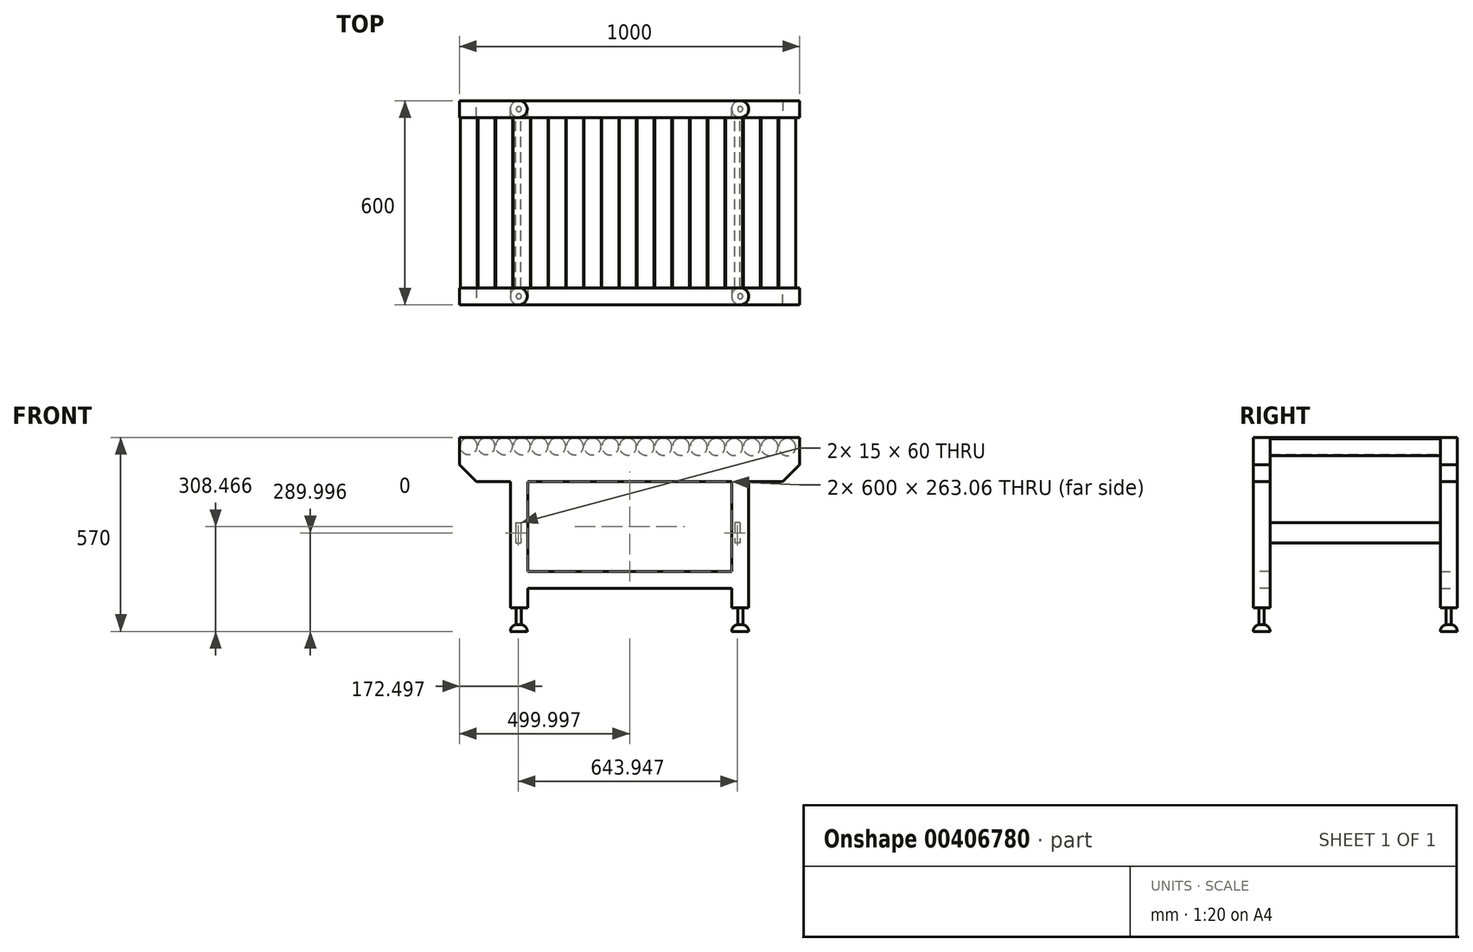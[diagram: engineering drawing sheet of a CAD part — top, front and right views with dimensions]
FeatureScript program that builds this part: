
annotation { "Feature Type Name" : "Feature", "Feature Type Description" : "" }
export const myFeature = defineFeature(function(context is Context, id is Id, definition is map)
    precondition{}
    {
        {
            var Q0;
            Q0=qCreatedBy(makeId("Front.planeOp"),FACE);
            var sketch = newSketch(context, id + "F0", { "sketchPlane" : qUnion([Q0])});
            skLineSegment(sketch, "E0", {"start": v(-494.47, 46.27) * mm, "end": v(505.53, 46.27) * mm});
            skLineSegment(sketch, "E1", {"start": v(505.53, 46.27) * mm, "end": v(505.53, -83.73) * mm});
            skLineSegment(sketch, "E2", {"start": v(505.53, -83.73) * mm, "end": v(355.53, -83.73) * mm});
            skLineSegment(sketch, "E3", {"start": v(355.53, -83.73) * mm, "end": v(355.53, -453.73) * mm});
            skLineSegment(sketch, "E4", {"start": v(355.53, -453.73) * mm, "end": v(305.53, -453.73) * mm});
            skLineSegment(sketch, "E5", {"start": v(305.53, -453.73) * mm, "end": v(305.53, -396.8) * mm});
            skLineSegment(sketch, "E6", {"start": v(305.53, -396.8) * mm, "end": v(-294.47, -396.8) * mm});
            skLineSegment(sketch, "E7", {"start": v(-294.47, -396.8) * mm, "end": v(-294.47, -453.73) * mm});
            skLineSegment(sketch, "E8", {"start": v(-294.47, -453.73) * mm, "end": v(-344.47, -453.73) * mm});
            skLineSegment(sketch, "E9", {"start": v(-344.47, -83.73) * mm, "end": v(-494.47, -83.73) * mm});
            skLineSegment(sketch, "E10", {"start": v(-494.47, -83.73) * mm, "end": v(-494.47, 46.27) * mm});
            skLineSegment(sketch, "E11", {"start": v(-344.47, -83.73) * mm, "end": v(-344.47, -453.73) * mm});
            skLineSegment(sketch, "E12.bottom", {"start": v(-294.47, -83.73) * mm, "end": v(305.53, -83.73) * mm});
            skLineSegment(sketch, "E12.top", {"start": v(-294.47, -346.8) * mm, "end": v(305.53, -346.8) * mm});
            skLineSegment(sketch, "E12.left", {"start": v(-294.47, -83.73) * mm, "end": v(-294.47, -346.8) * mm});
            skLineSegment(sketch, "E12.right", {"start": v(305.53, -83.73) * mm, "end": v(305.53, -346.8) * mm});
            skSolve(sketch);
        }
        {
            var Q0;
            Q0=makeQuery(id+"F0.imprint","IMPRINT",FACE,{"disambiguationData":[TD([[makeQuery(id+"F0.imprint","IMPRINT",EDGE,{"derivedFrom":sQuery(id+"F0.wireOp",EDGE,"E0")}),-1.0]])]});
            extrude(context, id + "F1", {"entities" : qUnion([Q0]), "depth" : 50 * mm});
        }
        {
            var Q0;
            Q0=makeQuery(id+"F1.opExtrude","SWEPT_EDGE",EDGE,{"disambiguationData":[OSD([sQuery(id+"F0.wireOp",EDGE,"E1"),sQuery(id+"F0.wireOp",EDGE,"E2")])]});
            chamfer(context, id + "F2", {"entities" : qUnion([Q0]), "width" : 50 * mm, "tangentPropagation" : true});
        }
        {
            var Q0;
            Q0=makeQuery(id+"F1.opExtrude","SWEPT_EDGE",EDGE,{"disambiguationData":[OSD([sQuery(id+"F0.wireOp",EDGE,"E9"),sQuery(id+"F0.wireOp",EDGE,"E10")])]});
            chamfer(context, id + "F3", {"entities" : qUnion([Q0]), "width" : 50 * mm, "tangentPropagation" : true});
        }
        {
            var Q0;
            Q0=makeQuery(id+"F1.opExtrude","CAP_FACE",FACE,{"disambiguationData":[OSD([sQuery(id+"F0.wireOp",EDGE,"E0"),sQuery(id+"F0.wireOp",EDGE,"E1"),sQuery(id+"F0.wireOp",EDGE,"E2"),sQuery(id+"F0.wireOp",EDGE,"E3"),sQuery(id+"F0.wireOp",EDGE,"E4"),sQuery(id+"F0.wireOp",EDGE,"E5"),sQuery(id+"F0.wireOp",EDGE,"E6"),sQuery(id+"F0.wireOp",EDGE,"E7"),sQuery(id+"F0.wireOp",EDGE,"E8"),sQuery(id+"F0.wireOp",EDGE,"E9"),sQuery(id+"F0.wireOp",EDGE,"E10"),sQuery(id+"F0.wireOp",EDGE,"E11"),sQuery(id+"F0.wireOp",EDGE,"E12.bottom"),sQuery(id+"F0.wireOp",EDGE,"E12.top"),sQuery(id+"F0.wireOp",EDGE,"E12.left"),sQuery(id+"F0.wireOp",EDGE,"E12.right")])],"isStart":false});
            var sketch = newSketch(context, id + "F4", { "sketchPlane" : qUnion([Q0])});
            skCircle(sketch, "E13", {"center": v(-467.47, 21.27) * mm, "radius": 25 * mm});
            skCircle(sketch, "E14.1.0.0", {"center": v(-415.47, 21.08) * mm, "radius": 25 * mm});
            skCircle(sketch, "E14.2.0.0", {"center": v(-363.47, 20.9) * mm, "radius": 25 * mm});
            skCircle(sketch, "E14.3.0.0", {"center": v(-311.47, 20.72) * mm, "radius": 25 * mm});
            skCircle(sketch, "E14.4.0.0", {"center": v(-259.47, 20.53) * mm, "radius": 25 * mm});
            skCircle(sketch, "E14.5.0.0", {"center": v(-207.47, 20.35) * mm, "radius": 25 * mm});
            skCircle(sketch, "E14.6.0.0", {"center": v(-155.48, 20.17) * mm, "radius": 25 * mm});
            skCircle(sketch, "E14.7.0.0", {"center": v(-103.48, 19.98) * mm, "radius": 25 * mm});
            skCircle(sketch, "E14.8.0.0", {"center": v(-51.48, 19.8) * mm, "radius": 25 * mm});
            skCircle(sketch, "E14.9.0.0", {"center": v(0.52, 19.62) * mm, "radius": 25 * mm});
            skCircle(sketch, "E14.10.0.0", {"center": v(52.52, 19.43) * mm, "radius": 25 * mm});
            skCircle(sketch, "E14.11.0.0", {"center": v(104.52, 19.25) * mm, "radius": 25 * mm});
            skCircle(sketch, "E14.12.0.0", {"center": v(156.52, 19.06) * mm, "radius": 25 * mm});
            skCircle(sketch, "E14.13.0.0", {"center": v(208.52, 18.88) * mm, "radius": 25 * mm});
            skCircle(sketch, "E14.14.0.0", {"center": v(260.52, 18.7) * mm, "radius": 25 * mm});
            skCircle(sketch, "E14.15.0.0", {"center": v(312.52, 18.51) * mm, "radius": 25 * mm});
            skCircle(sketch, "E14.16.0.0", {"center": v(364.52, 18.33) * mm, "radius": 25 * mm});
            skCircle(sketch, "E14.17.0.0", {"center": v(416.52, 18.15) * mm, "radius": 25 * mm});
            skCircle(sketch, "E14.18.0.0", {"center": v(468.52, 17.96) * mm, "radius": 25 * mm});
            skLineSegment(sketch, "E14.direction1", {"start": v(-467.47, 21.27) * mm, "end": v(-415.47, 21.08) * mm, "construction": true});
            skSolve(sketch);
        }
        {
            var Q0;
            Q0=makeQuery(id+"F4.imprint","IMPRINT",FACE,{"disambiguationData":[TD([[makeQuery(id+"F4.imprint","IMPRINT",EDGE,{"derivedFrom":sQuery(id+"F4.wireOp",EDGE,"E13")}),1.0]])]});
            var Q1;
            Q1=makeQuery(id+"F4.imprint","IMPRINT",FACE,{"disambiguationData":[TD([[makeQuery(id+"F4.imprint","IMPRINT",EDGE,{"derivedFrom":sQuery(id+"F4.wireOp",EDGE,"E14.1.0.0")}),1.0]])]});
            var Q2;
            Q2=makeQuery(id+"F4.imprint","IMPRINT",FACE,{"disambiguationData":[TD([[makeQuery(id+"F4.imprint","IMPRINT",EDGE,{"derivedFrom":sQuery(id+"F4.wireOp",EDGE,"E14.2.0.0")}),1.0]])]});
            var Q3;
            Q3=makeQuery(id+"F4.imprint","IMPRINT",FACE,{"disambiguationData":[TD([[makeQuery(id+"F4.imprint","IMPRINT",EDGE,{"derivedFrom":sQuery(id+"F4.wireOp",EDGE,"E14.3.0.0")}),1.0]])]});
            var Q4;
            Q4=makeQuery(id+"F4.imprint","IMPRINT",FACE,{"disambiguationData":[TD([[makeQuery(id+"F4.imprint","IMPRINT",EDGE,{"derivedFrom":sQuery(id+"F4.wireOp",EDGE,"E14.4.0.0")}),1.0]])]});
            var Q5;
            Q5=makeQuery(id+"F4.imprint","IMPRINT",FACE,{"disambiguationData":[TD([[makeQuery(id+"F4.imprint","IMPRINT",EDGE,{"derivedFrom":sQuery(id+"F4.wireOp",EDGE,"E14.5.0.0")}),1.0]])]});
            var Q6;
            Q6=makeQuery(id+"F4.imprint","IMPRINT",FACE,{"disambiguationData":[TD([[makeQuery(id+"F4.imprint","IMPRINT",EDGE,{"derivedFrom":sQuery(id+"F4.wireOp",EDGE,"E14.6.0.0")}),1.0]])]});
            var Q7;
            Q7=makeQuery(id+"F4.imprint","IMPRINT",FACE,{"disambiguationData":[TD([[makeQuery(id+"F4.imprint","IMPRINT",EDGE,{"derivedFrom":sQuery(id+"F4.wireOp",EDGE,"E14.7.0.0")}),1.0]])]});
            var Q8;
            Q8=makeQuery(id+"F4.imprint","IMPRINT",FACE,{"disambiguationData":[TD([[makeQuery(id+"F4.imprint","IMPRINT",EDGE,{"derivedFrom":sQuery(id+"F4.wireOp",EDGE,"E14.8.0.0")}),1.0]])]});
            var Q9;
            Q9=makeQuery(id+"F4.imprint","IMPRINT",FACE,{"disambiguationData":[TD([[makeQuery(id+"F4.imprint","IMPRINT",EDGE,{"derivedFrom":sQuery(id+"F4.wireOp",EDGE,"E14.9.0.0")}),1.0]])]});
            var Q10;
            Q10=makeQuery(id+"F4.imprint","IMPRINT",FACE,{"disambiguationData":[TD([[makeQuery(id+"F4.imprint","IMPRINT",EDGE,{"derivedFrom":sQuery(id+"F4.wireOp",EDGE,"E14.10.0.0")}),1.0]])]});
            var Q11;
            Q11=makeQuery(id+"F4.imprint","IMPRINT",FACE,{"disambiguationData":[TD([[makeQuery(id+"F4.imprint","IMPRINT",EDGE,{"derivedFrom":sQuery(id+"F4.wireOp",EDGE,"E14.11.0.0")}),1.0]])]});
            var Q12;
            Q12=makeQuery(id+"F4.imprint","IMPRINT",FACE,{"disambiguationData":[TD([[makeQuery(id+"F4.imprint","IMPRINT",EDGE,{"derivedFrom":sQuery(id+"F4.wireOp",EDGE,"E14.12.0.0")}),1.0]])]});
            var Q13;
            Q13=makeQuery(id+"F4.imprint","IMPRINT",FACE,{"disambiguationData":[TD([[makeQuery(id+"F4.imprint","IMPRINT",EDGE,{"derivedFrom":sQuery(id+"F4.wireOp",EDGE,"E14.13.0.0")}),1.0]])]});
            var Q14;
            Q14=makeQuery(id+"F4.imprint","IMPRINT",FACE,{"disambiguationData":[TD([[makeQuery(id+"F4.imprint","IMPRINT",EDGE,{"derivedFrom":sQuery(id+"F4.wireOp",EDGE,"E14.14.0.0")}),1.0]])]});
            var Q15;
            Q15=makeQuery(id+"F4.imprint","IMPRINT",FACE,{"disambiguationData":[TD([[makeQuery(id+"F4.imprint","IMPRINT",EDGE,{"derivedFrom":sQuery(id+"F4.wireOp",EDGE,"E14.15.0.0")}),1.0]])]});
            var Q16;
            Q16=makeQuery(id+"F4.imprint","IMPRINT",FACE,{"disambiguationData":[TD([[makeQuery(id+"F4.imprint","IMPRINT",EDGE,{"derivedFrom":sQuery(id+"F4.wireOp",EDGE,"E14.16.0.0")}),1.0]])]});
            var Q17;
            Q17=makeQuery(id+"F4.imprint","IMPRINT",FACE,{"disambiguationData":[TD([[makeQuery(id+"F4.imprint","IMPRINT",EDGE,{"derivedFrom":sQuery(id+"F4.wireOp",EDGE,"E14.17.0.0")}),1.0]])]});
            var Q18;
            Q18=makeQuery(id+"F4.imprint","IMPRINT",FACE,{"disambiguationData":[TD([[makeQuery(id+"F4.imprint","IMPRINT",EDGE,{"derivedFrom":sQuery(id+"F4.wireOp",EDGE,"E14.18.0.0")}),1.0]])]});
            extrude(context, id + "F5", {"entities" : qUnion([Q0, Q1, Q2, Q3, Q4, Q5, Q6, Q7, Q8, Q9, Q10, Q11, Q12, Q13, Q14, Q15, Q16, Q17, Q18]), "operationType" : NewBodyOperationType.ADD, "depth" : 250 * mm});
        }
        {
            var Q0;
            Q0=makeQuery(id+"F1.opExtrude","SWEPT_FACE",FACE,{"disambiguationData":[OSD([sQuery(id+"F0.wireOp",EDGE,"E4")])]});
            var sketch = newSketch(context, id + "F6", { "sketchPlane" : qUnion([Q0])});
            skPoint(sketch, "E15.startSnap0", {"position": v(330.53, 50) * mm});
            skPoint(sketch, "E15.startSnap1", {"position": v(305.53, 25) * mm});
            skCircle(sketch, "E16", {"center": v(330.53, 25) * mm, "radius": 7.5 * mm});
            skCircle(sketch, "E17", {"center": v(-320.34, 25) * mm, "radius": 7.5 * mm});
            skSolve(sketch);
        }
        {
            var Q0;
            Q0=makeQuery(id+"F6.imprint","IMPRINT",FACE,{"disambiguationData":[TD([[makeQuery(id+"F6.imprint","IMPRINT",EDGE,{"derivedFrom":sQuery(id+"F6.wireOp",EDGE,"E17")}),1.0]])]});
            var Q1;
            Q1=makeQuery(id+"F6.imprint","IMPRINT",FACE,{"disambiguationData":[TD([[makeQuery(id+"F6.imprint","IMPRINT",EDGE,{"derivedFrom":sQuery(id+"F6.wireOp",EDGE,"E16")}),1.0]])]});
            extrude(context, id + "F7", {"entities" : qUnion([Q0, Q1]), "operationType" : NewBodyOperationType.ADD, "depth" : 50 * mm});
        }
        {
            var Q0;
            Q0=makeQuery(id+"F1.opExtrude","CAP_FACE",FACE,{"disambiguationData":[OSD([sQuery(id+"F0.wireOp",EDGE,"E0"),sQuery(id+"F0.wireOp",EDGE,"E1"),sQuery(id+"F0.wireOp",EDGE,"E2"),sQuery(id+"F0.wireOp",EDGE,"E3"),sQuery(id+"F0.wireOp",EDGE,"E4"),sQuery(id+"F0.wireOp",EDGE,"E5"),sQuery(id+"F0.wireOp",EDGE,"E6"),sQuery(id+"F0.wireOp",EDGE,"E7"),sQuery(id+"F0.wireOp",EDGE,"E8"),sQuery(id+"F0.wireOp",EDGE,"E9"),sQuery(id+"F0.wireOp",EDGE,"E10"),sQuery(id+"F0.wireOp",EDGE,"E11"),sQuery(id+"F0.wireOp",EDGE,"E12.bottom"),sQuery(id+"F0.wireOp",EDGE,"E12.top"),sQuery(id+"F0.wireOp",EDGE,"E12.left"),sQuery(id+"F0.wireOp",EDGE,"E12.right")])],"isStart":false});
            var sketch = newSketch(context, id + "F8", { "sketchPlane" : qUnion([Q0])});
            skLineSegment(sketch, "E18.bottom", {"start": v(-329.47, -203.73) * mm, "end": v(-314.47, -203.73) * mm});
            skLineSegment(sketch, "E18.top", {"start": v(-329.47, -263.73) * mm, "end": v(-314.47, -263.73) * mm});
            skLineSegment(sketch, "E18.left", {"start": v(-329.47, -203.73) * mm, "end": v(-329.47, -263.73) * mm});
            skLineSegment(sketch, "E18.right", {"start": v(-314.47, -203.73) * mm, "end": v(-314.47, -263.73) * mm});
            skLineSegment(sketch, "E19", {"start": v(0, -303.64) * mm, "end": v(0, -135.55) * mm});
            skLineSegment(sketch, "E20.MirrorCS", {"start": v(329.47, -203.73) * mm, "end": v(329.47, -263.73) * mm});
            skLineSegment(sketch, "E21.MirrorCS", {"start": v(329.47, -203.73) * mm, "end": v(314.47, -203.73) * mm});
            skLineSegment(sketch, "E22.MirrorCS", {"start": v(329.47, -263.73) * mm, "end": v(314.47, -263.73) * mm});
            skLineSegment(sketch, "E23.MirrorCS", {"start": v(314.47, -203.73) * mm, "end": v(314.47, -263.73) * mm});
            skSolve(sketch);
        }
        {
            var Q0;
            Q0=makeQuery(id+"F8.imprint","IMPRINT",FACE,{"disambiguationData":[TD([[makeQuery(id+"F8.imprint","IMPRINT",EDGE,{"derivedFrom":sQuery(id+"F8.wireOp",EDGE,"E18.bottom")}),-1.0]])]});
            var Q1;
            Q1=makeQuery(id+"F8.imprint","IMPRINT",FACE,{"disambiguationData":[TD([[makeQuery(id+"F8.imprint","IMPRINT",EDGE,{"derivedFrom":sQuery(id+"F8.wireOp",EDGE,"E20.MirrorCS")}),-1.0]])]});
            extrude(context, id + "F9", {"entities" : qUnion([Q0, Q1]), "operationType" : NewBodyOperationType.ADD, "depth" : 250 * mm});
        }
        {
            var Q0;
            Q0=makeQuery(id+"F7.opExtrude","CAP_FACE",FACE,{"disambiguationData":[OSD([sQuery(id+"F6.wireOp",EDGE,"E17")])],"isStart":false});
            var sketch = newSketch(context, id + "F10", { "sketchPlane" : qUnion([Q0])});
            skCircle(sketch, "E24", {"center": v(330.53, 25) * mm, "radius": 25 * mm});
            skCircle(sketch, "E25", {"center": v(-320.34, 25) * mm, "radius": 25 * mm});
            skSolve(sketch);
        }
        {
            var Q0;
            Q0=makeQuery(id+"F10.imprint","IMPRINT",FACE,{"disambiguationData":[TD([[makeQuery(id+"F10.imprint","IMPRINT",EDGE,{"derivedFrom":sQuery(id+"F10.wireOp",EDGE,"E25")}),1.0]])]});
            var Q1;
            Q1=makeQuery(id+"F10.imprint","IMPRINT",FACE,{"disambiguationData":[TD([[makeQuery(id+"F10.imprint","IMPRINT",EDGE,{"derivedFrom":makeQuery(id+"F7.opExtrude","CAP_EDGE",EDGE,{"disambiguationData":[OSD([sQuery(id+"F6.wireOp",EDGE,"E17")])],"isStart":false})}),1.0]])]});
            var Q2;
            Q2=makeQuery(id+"F10.imprint","IMPRINT",FACE,{"disambiguationData":[TD([[makeQuery(id+"F10.imprint","IMPRINT",EDGE,{"derivedFrom":sQuery(id+"F10.wireOp",EDGE,"E24")}),1.0]])]});
            extrude(context, id + "F11", {"entities" : qUnion([Q0, Q1, Q2]), "operationType" : NewBodyOperationType.ADD, "depth" : 20 * mm});
        }
        {
            var Q0;
            Q0=makeQuery(id+"F11.opExtrude","CAP_EDGE",EDGE,{"disambiguationData":[OSD([sQuery(id+"F10.wireOp",EDGE,"E25")])],"isStart":true});
            var Q1;
            Q1=makeQuery(id+"F11.opExtrude","CAP_EDGE",EDGE,{"disambiguationData":[OSD([sQuery(id+"F10.wireOp",EDGE,"E24")])],"isStart":true});
            fillet(context, id + "F12", {"entities" : qUnion([Q0, Q1]), "radius" : 20 * mm, "tangentPropagation" : true, "allowEdgeOverflow" : false});
        }
        {
            var Q0;
            Q0=makeQuery(id+"F1.opExtrude","SWEPT_BODY",BODY,{"disambiguationData":[OSD([sQuery(id+"F0.wireOp",EDGE,"E0"),sQuery(id+"F0.wireOp",EDGE,"E1"),sQuery(id+"F0.wireOp",EDGE,"E2"),sQuery(id+"F0.wireOp",EDGE,"E3"),sQuery(id+"F0.wireOp",EDGE,"E4"),sQuery(id+"F0.wireOp",EDGE,"E5"),sQuery(id+"F0.wireOp",EDGE,"E6"),sQuery(id+"F0.wireOp",EDGE,"E7"),sQuery(id+"F0.wireOp",EDGE,"E8"),sQuery(id+"F0.wireOp",EDGE,"E9"),sQuery(id+"F0.wireOp",EDGE,"E10"),sQuery(id+"F0.wireOp",EDGE,"E11"),sQuery(id+"F0.wireOp",EDGE,"E12.bottom"),sQuery(id+"F0.wireOp",EDGE,"E12.top"),sQuery(id+"F0.wireOp",EDGE,"E12.left"),sQuery(id+"F0.wireOp",EDGE,"E12.right")])]});
            var Q1;
            Q1=makeQuery(id+"F5.opExtrude","CAP_FACE",FACE,{"disambiguationData":[OSD([sQuery(id+"F4.wireOp",EDGE,"E14.11.0.0")])],"isStart":false});
            mirror(context, id + "F13", {"operationType" : NewBodyOperationType.ADD, "entities" : qUnion([Q0]), "mirrorPlane" : qUnion([Q1])});
        }
    });
